FCSTD DOCUMENT  (FreeCAD 0.20R)
Label: pluto_p53_holder
License: All rights reserved
LicenseURL: http://en.wikipedia.org/wiki/All_rights_reserved
objects: Part::Box×4, Part::Cylinder×4, Part::Cut×4, Part::MultiFuse×3, Part::Feature×2, Sketcher::SketchObject×2, Part::Extrusion×2, Mesh::Feature×1
note: 21 computed .brp shape members not serialized (recipe doc carries the construction recipe); baked Part::Feature solids carry a one-line shape summary decoded from their .brp

FEATURE [Mesh::Feature] Pluto_Holder_Uni_v1_1_DM4DS  label="Pluto_Holder_Uni_v1.1_DM4DS"
FEATURE [Part::Box] Box  label="Cube"
  AttacherType = Attacher::AttachEngine3D
  Height = 7
  Length = 32
  Placement = pos=(-58,-43,0) rot=(0,0,1;0rad)
  Width = 10
FEATURE [Part::Cylinder] Cylinder
  Angle = 360
  AttacherType = Attacher::AttachEngine3D
  FirstAngle = 0
  Height = 20
  Placement = pos=(-58,-38,3.5) rot=(0,1,0;1.5708rad)
  Radius = 2
  SecondAngle = 0
FEATURE [Part::Cut] Cut
  Base = -> Box
  Tool = -> Cylinder
FEATURE [Part::Box] Box001  label="Cube001"
  AttacherType = Attacher::AttachEngine3D
  Height = 7
  Length = 32
  Placement = pos=(-58,33,0) rot=(0,0,1;0rad)
  Width = 10
FEATURE [Part::Cylinder] Cylinder001
  Angle = 360
  AttacherType = Attacher::AttachEngine3D
  FirstAngle = 0
  Height = 20
  Placement = pos=(-58,38,3.5) rot=(0,1,0;1.5708rad)
  Radius = 2
  SecondAngle = 0
FEATURE [Part::Cut] Cut001
  Base = -> Box001
  Tool = -> Cylinder001
FEATURE [Part::Feature] Pluto_Holder_Uni_v1_1_DM4DS001
  shape: large baked B-rep (37 MB .brp); summary skipped
FEATURE [Part::Feature] Pluto_Holder_Uni_v1_1_DM4DS001_solid  label="Pluto_Holder_Uni_v1_1_DM4DS001 (Solid)"
  shape: large baked B-rep (37 MB .brp); summary skipped
FEATURE [Part::MultiFuse] Fusion
  Shapes = -> [Pluto_Holder_Uni_v1_1_DM4DS001_solid,Cut001,Cut]
FEATURE [Part::Box] Box002  label="Cube002"
  AttacherType = Attacher::AttachEngine3D
  Height = 18
  Length = 5
  Placement = pos=(-63,-43,-11) rot=(0,0,1;0rad)
  Width = 10
FEATURE [Sketcher::SketchObject] Sketch
  FullyConstrained = false
  Placement = pos=(0,0,0) rot=(1,0,0;1.5708rad)
  sketch-geometry (5):
    g0: LineSegment StartX=-49.2246 StartY=-10.0835 StartZ=0 EndX=-33.2246 EndY=-10.0835 EndZ=0
    g1: LineSegment StartX=-33.2246 StartY=-10.0835 StartZ=0 EndX=-33.2246 EndY=-6.31349 EndZ=0
    g2: LineSegment StartX=-33.2246 StartY=-6.31349 StartZ=0 EndX=-35.2246 EndY=-6.31349 EndZ=0
    g3: LineSegment StartX=-49.2246 StartY=-10.0835 StartZ=0 EndX=-49.2246 EndY=-7.31349 EndZ=0
    g4: LineSegment StartX=-35.2246 StartY=-6.31349 StartZ=0 EndX=-49.2246 EndY=-7.31349 EndZ=0
  constraints (13):
    c: Horizontal(g0)
    c: DistanceX(g0,g0) = 16
    c: Coincident(g1,g0)
    c: Vertical(g1)
    c: DistanceY(g1,g1) = 3.77
    c: Coincident(g2,g1)
    c: Horizontal(g2)
    c: DistanceX(g2,g2) = 2
    c: Coincident(g3,g0)
    c: Vertical(g3)
    c: DistanceY(g3,g3) = 2.77
    c: Coincident(g4,g2)
    c: Coincident(g4,g3)
FEATURE [Part::Extrusion] Extrude
  Base = -> Sketch
  Dir = (0,-1,-3e-16)
  DirMode = 2
  FaceMakerClass = Part::FaceMakerBullseye
  LengthFwd = 10
  LengthRev = 0
  Placement = pos=(-8.77542,-33,-0.916505) rot=(0,0,1;0rad)
  Solid = true
  Symmetric = false
FEATURE [Part::Cylinder] Cylinder002
  Angle = 360
  AttacherType = Attacher::AttachEngine3D
  FirstAngle = 0
  Height = 10
  Placement = pos=(-65,-38,3.5) rot=(0,1,0;1.5708rad)
  Radius = 2
  SecondAngle = 0
FEATURE [Part::Cut] Cut002
  Base = -> Box002
  Tool = -> Cylinder002
FEATURE [Part::MultiFuse] Fusion001
  Shapes = -> [Extrude,Cut002]
FEATURE [Part::Box] Box003  label="Cube003"
  AttacherType = Attacher::AttachEngine3D
  Height = 18
  Length = 5
  Placement = pos=(-63,-43,-11) rot=(0,0,1;0rad)
  Width = 10
FEATURE [Part::Cylinder] Cylinder003
  Angle = 360
  AttacherType = Attacher::AttachEngine3D
  FirstAngle = 0
  Height = 10
  Placement = pos=(-65,-38,3.5) rot=(0,1,0;1.5708rad)
  Radius = 2
  SecondAngle = 0
FEATURE [Part::Cut] Cut003
  Base = -> Box003
  Tool = -> Cylinder003
FEATURE [Sketcher::SketchObject] Sketch001
  FullyConstrained = false
  Placement = pos=(0,0,0) rot=(1,0,0;1.5708rad)
  sketch-geometry (5):
    g0: LineSegment StartX=-49.2246 StartY=-10.0835 StartZ=0 EndX=-33.2246 EndY=-10.0835 EndZ=0
    g1: LineSegment StartX=-33.2246 StartY=-10.0835 StartZ=0 EndX=-33.2246 EndY=-6.31349 EndZ=0
    g2: LineSegment StartX=-33.2246 StartY=-6.31349 StartZ=0 EndX=-35.2246 EndY=-6.31349 EndZ=0
    g3: LineSegment StartX=-49.2246 StartY=-10.0835 StartZ=0 EndX=-49.2246 EndY=-7.31349 EndZ=0
    g4: LineSegment StartX=-35.2246 StartY=-6.31349 StartZ=0 EndX=-49.2246 EndY=-7.31349 EndZ=0
  constraints (13):
    c: Horizontal(g0)
    c: DistanceX(g0,g0) = 16
    c: Coincident(g1,g0)
    c: Vertical(g1)
    c: DistanceY(g1,g1) = 3.77
    c: Coincident(g2,g1)
    c: Horizontal(g2)
    c: DistanceX(g2,g2) = 2
    c: Coincident(g3,g0)
    c: Vertical(g3)
    c: DistanceY(g3,g3) = 2.77
    c: Coincident(g4,g2)
    c: Coincident(g4,g3)
FEATURE [Part::Extrusion] Extrude001
  Base = -> Sketch001
  Dir = (0,-1,-3e-16)
  DirMode = 2
  FaceMakerClass = Part::FaceMakerBullseye
  LengthFwd = 10
  LengthRev = 0
  Placement = pos=(-8.77542,-33,-0.916505) rot=(0,0,1;0rad)
  Solid = true
  Symmetric = false
FEATURE [Part::MultiFuse] Fusion002
  Placement = pos=(0,76,0) rot=(0,0,1;0rad)
  Shapes = -> [Extrude001,Cut003]
